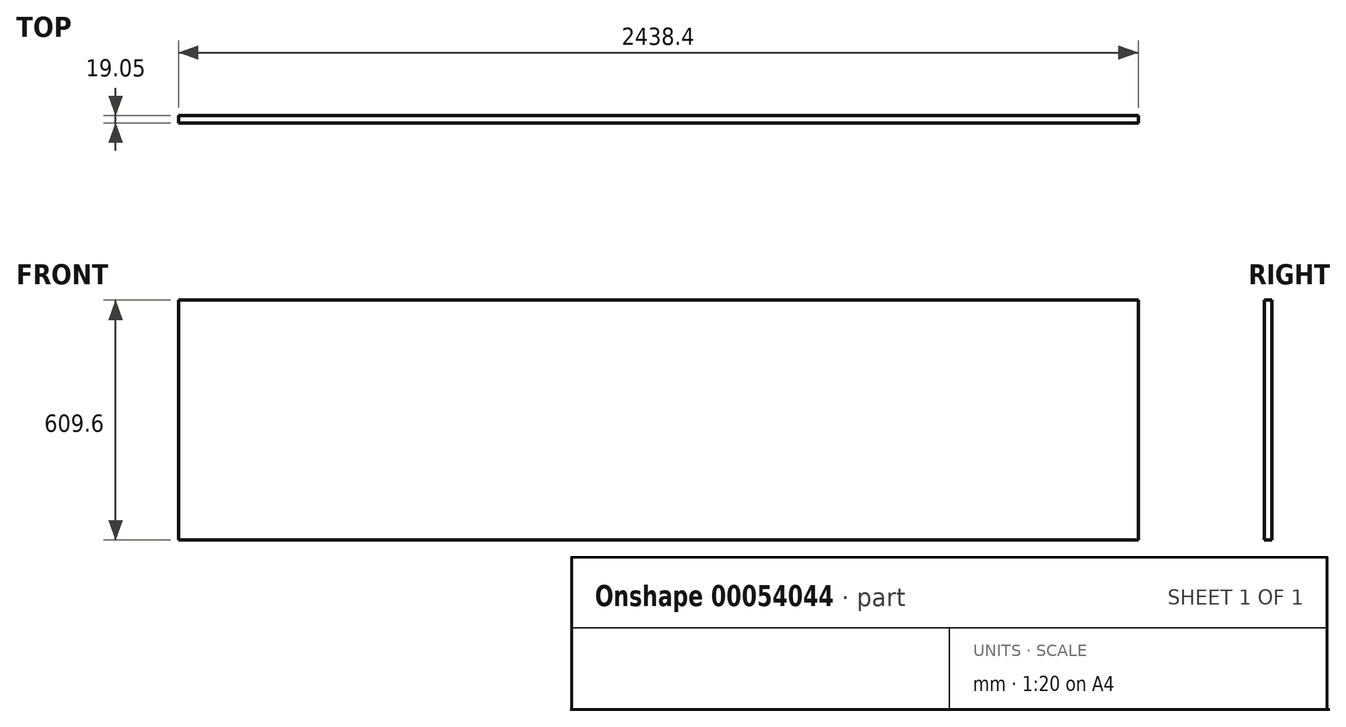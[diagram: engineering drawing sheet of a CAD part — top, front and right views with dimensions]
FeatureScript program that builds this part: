
annotation { "Feature Type Name" : "Feature", "Feature Type Description" : "" }
export const myFeature = defineFeature(function(context is Context, id is Id, definition is map)
    precondition{}
    {
        {
            var Q0;
            Q0=qCreatedBy(makeId("Front.planeOp"),FACE);
            var sketch = newSketch(context, id + "F0", { "sketchPlane" : qUnion([Q0])});
            skLineSegment(sketch, "E0.bottom", {"start": v(2.44, 0) * mm, "end": v(2440.84, 0) * mm});
            skLineSegment(sketch, "E0.top", {"start": v(2.44, 609.6) * mm, "end": v(2440.84, 609.6) * mm});
            skLineSegment(sketch, "E0.left", {"start": v(2.44, 0) * mm, "end": v(2.44, 609.6) * mm});
            skLineSegment(sketch, "E0.right", {"start": v(2440.84, 0) * mm, "end": v(2440.84, 609.6) * mm});
            skSolve(sketch);
        }
        {
            var Q0;
            Q0=makeQuery(id+"F0.imprint","IMPRINT",FACE,{"disambiguationData":[TD([[makeQuery(id+"F0.imprint","IMPRINT",EDGE,{"derivedFrom":sQuery(id+"F0.wireOp",EDGE,"E0.bottom")}),1.0]])]});
            extrude(context, id + "F1", {"entities" : qUnion([Q0]), "depth" : 19.05 * mm});
        }
    });
